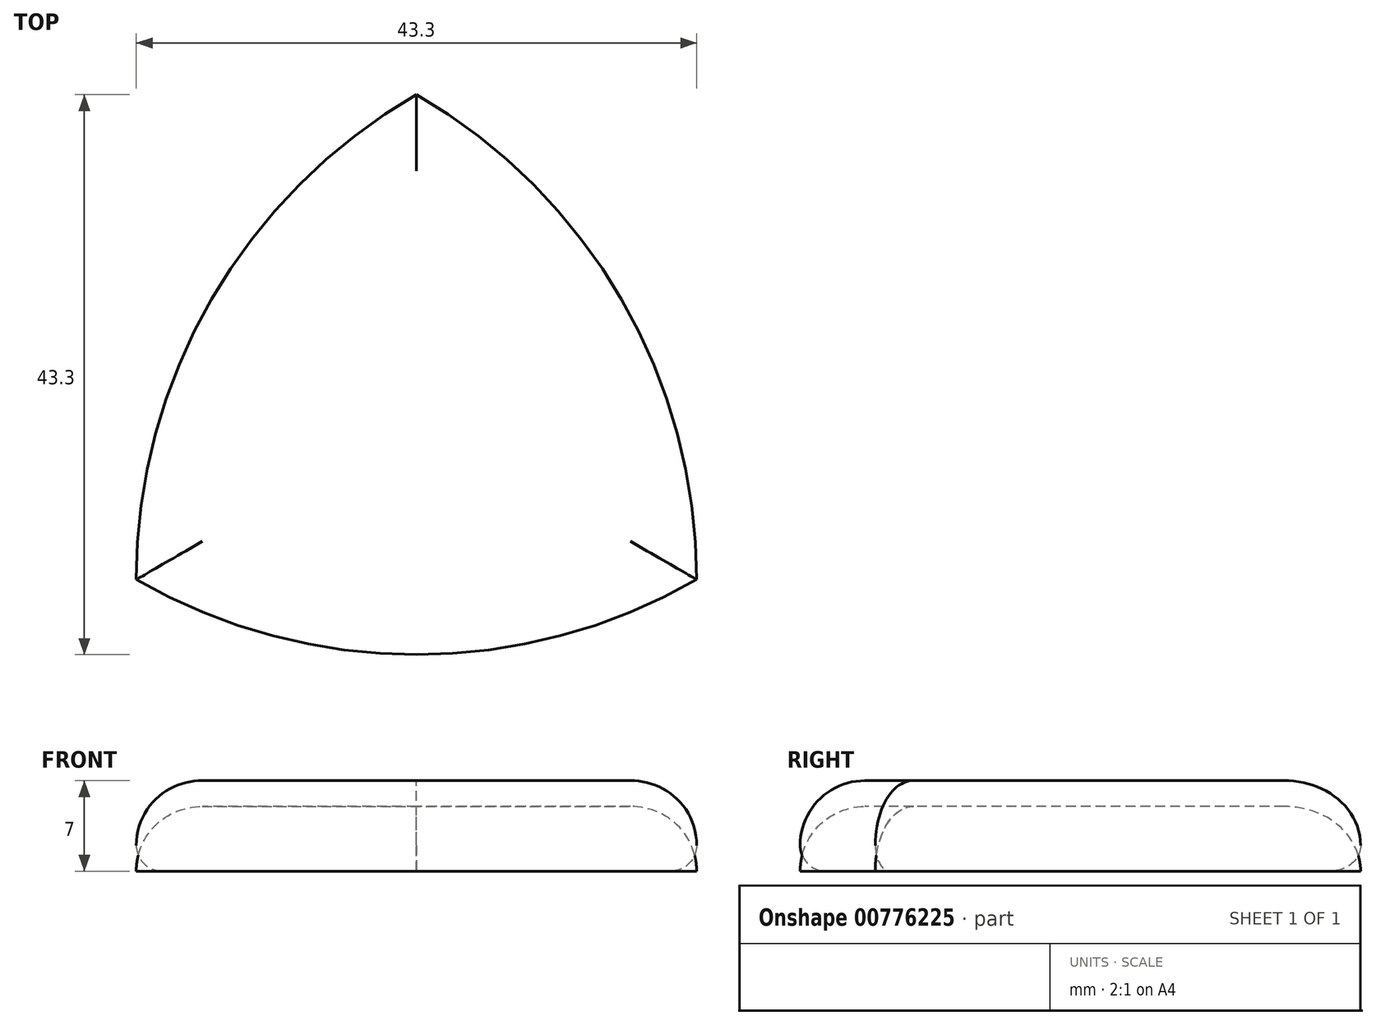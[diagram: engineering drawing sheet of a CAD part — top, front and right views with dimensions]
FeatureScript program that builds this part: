
annotation { "Feature Type Name" : "Feature", "Feature Type Description" : "" }
export const myFeature = defineFeature(function(context is Context, id is Id, definition is map)
    precondition{}
    {
        {
            var Q0;
            Q0=qCreatedBy(makeId("Top.planeOp"),FACE);
            var sketch = newSketch(context, id + "F0", { "sketchPlane" : qUnion([Q0])});
            skArc(sketch, "E0", {"start": v(21.65, -12.5) * mm, "mid": v(15.85, 9.15) * mm, "end": v(0, 25) * mm});
            skArc(sketch, "E1", {"start": v(0, 25) * mm, "mid": v(-15.85, 9.15) * mm, "end": v(-21.65, -12.5) * mm});
            skArc(sketch, "E2", {"start": v(-21.65, -12.5) * mm, "mid": v(0, -18.3) * mm, "end": v(21.65, -12.5) * mm});
            skSolve(sketch);
        }
        {
            var Q0;
            Q0=makeQuery(id+"F0.imprint","IMPRINT",FACE,{"disambiguationData":[TD([[makeQuery(id+"F0.imprint","IMPRINT",EDGE,{"derivedFrom":sQuery(id+"F0.wireOp",EDGE,"E0")}),1.0]])]});
            extrude(context, id + "F1", {"entities" : qUnion([Q0]), "depth" : 5 * mm, "offsetDistance" : 25 * mm});
        }
        {
            var Q0;
            Q0=makeQuery(id+"F1.opExtrude","CAP_FACE",FACE,{"disambiguationData":[OSD([sQuery(id+"F0.wireOp",EDGE,"E0"),sQuery(id+"F0.wireOp",EDGE,"E1"),sQuery(id+"F0.wireOp",EDGE,"E2")])],"isStart":false});
            fillet(context, id + "F2", {"entities" : qUnion([Q0]), "radius" : 5 * mm, "tangentPropagation" : true, "allowEdgeOverflow" : false});
        }
        {
            var Q0;
            Q0=makeQuery(id+"F0.imprint","IMPRINT",FACE,{"disambiguationData":[TD([[makeQuery(id+"F0.imprint","IMPRINT",EDGE,{"derivedFrom":sQuery(id+"F0.wireOp",EDGE,"E0")}),1.0]])]});
            extrude(context, id + "F3", {"entities" : qUnion([Q0]), "depth" : 7 * mm, "offsetDistance" : 25 * mm});
        }
        {
            var Q0;
            Q0=makeQuery(id+"F3.opExtrude","CAP_FACE",FACE,{"disambiguationData":[OSD([sQuery(id+"F0.wireOp",EDGE,"E0"),sQuery(id+"F0.wireOp",EDGE,"E1"),sQuery(id+"F0.wireOp",EDGE,"E2")])],"isStart":false});
            fillet(context, id + "F4", {"entities" : qUnion([Q0]), "radius" : 5 * mm, "tangentPropagation" : true, "allowEdgeOverflow" : false});
        }
        {
            var Q0;
            Q0=makeQuery(id+"F3.opExtrude","CAP_FACE",FACE,{"disambiguationData":[OSD([sQuery(id+"F0.wireOp",EDGE,"E0"),sQuery(id+"F0.wireOp",EDGE,"E1"),sQuery(id+"F0.wireOp",EDGE,"E2")])],"isStart":true});
            fillet(context, id + "F5", {"entities" : qUnion([Q0]), "radius" : 2 * mm, "tangentPropagation" : true, "allowEdgeOverflow" : false});
        }
    });
